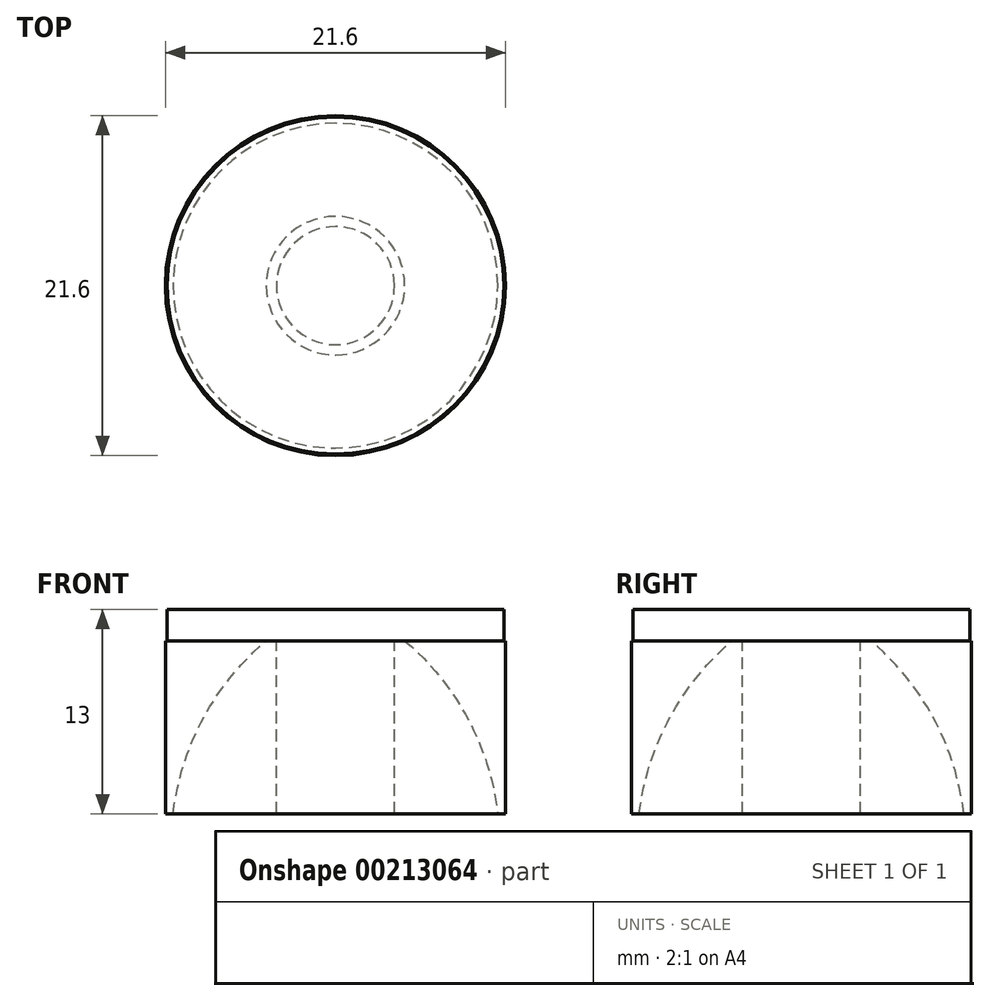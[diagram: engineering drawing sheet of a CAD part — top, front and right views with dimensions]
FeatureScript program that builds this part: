
annotation { "Feature Type Name" : "Feature", "Feature Type Description" : "" }
export const myFeature = defineFeature(function(context is Context, id is Id, definition is map)
    precondition{}
    {
        {
            var Q0;
            Q0=qCreatedBy(makeId("Top.planeOp"),FACE);
            var sketch = newSketch(context, id + "F0", { "sketchPlane" : qUnion([Q0])});
            skCircle(sketch, "E0", {"center": v(0, 0) * mm, "radius": 10.7 * mm});
            skSolve(sketch);
        }
        {
            var Q0;
            Q0=makeQuery(id+"F0.imprint","IMPRINT",FACE,{"disambiguationData":[TD([[makeQuery(id+"F0.imprint","IMPRINT",EDGE,{"derivedFrom":sQuery(id+"F0.wireOp",EDGE,"E0")}),1.0]])]});
            extrude(context, id + "F1", {"entities" : qUnion([Q0]), "depth" : 2 * mm});
        }
        {
            var Q0;
            Q0=qCreatedBy(makeId("Top.planeOp"),FACE);
            var sketch = newSketch(context, id + "F2", { "sketchPlane" : qUnion([Q0])});
            skCircle(sketch, "E1", {"center": v(0, 0) * mm, "radius": 3.75 * mm});
            skSolve(sketch);
        }
        {
            var Q0;
            Q0=makeQuery(id+"F2.imprint","IMPRINT",FACE,{"disambiguationData":[TD([[makeQuery(id+"F2.imprint","IMPRINT",EDGE,{"derivedFrom":sQuery(id+"F2.wireOp",EDGE,"E1")}),1.0]])]});
            var Q1;
            Q1=sQuery(id+"F2.wireOp",EDGE,"E1");
            extrude(context, id + "F3", {"entities" : qUnion([Q0]), "surfaceEntities" : qUnion([Q1]), "oppositeDirection" : true, "depth" : 11 * mm});
        }
        {
            var Q0;
            Q0=qCreatedBy(makeId("Front.planeOp"),FACE);
            var sketch = newSketch(context, id + "F4", { "sketchPlane" : qUnion([Q0])});
            skLineSegment(sketch, "E2", {"start": v(0, 17.84) * mm, "end": v(0, -26.69) * mm, "construction": true});
            skLineSegment(sketch, "E3", {"start": v(-10.8, 0) * mm, "end": v(-10.8, -11) * mm});
            skLineSegment(sketch, "E4", {"start": v(-10.8, 0) * mm, "end": v(-4.4, 0) * mm});
            skLineSegment(sketch, "E5", {"start": v(-10.8, -11) * mm, "end": v(-10.31, -11) * mm});
            skArc(sketch, "E6", {"start": v(-4.4, 0) * mm, "mid": v(-8.4, -4.94) * mm, "end": v(-10.31, -11) * mm});
            skLineSegment(sketch, "E7", {"start": v(-10.8, 0) * mm, "end": v(0, 0) * mm});
            skSolve(sketch);
        }
        {
            var Q0;
            Q0=makeQuery(id+"F4.imprint","IMPRINT",FACE,{"disambiguationData":[TD([[makeQuery(id+"F4.imprint","IMPRINT",EDGE,{"derivedFrom":sQuery(id+"F4.wireOp",EDGE,"E3")}),1.0]])]});
            var Q1;
            Q1=sQuery(id+"F4.wireOp",EDGE,"E2");
            revolve(context, id + "F5", {"operationType" : NewBodyOperationType.ADD, "entities" : qUnion([Q0]), "axis" : qUnion([Q1]), "revolveType" : RevolveType.FULL});
        }
    });
